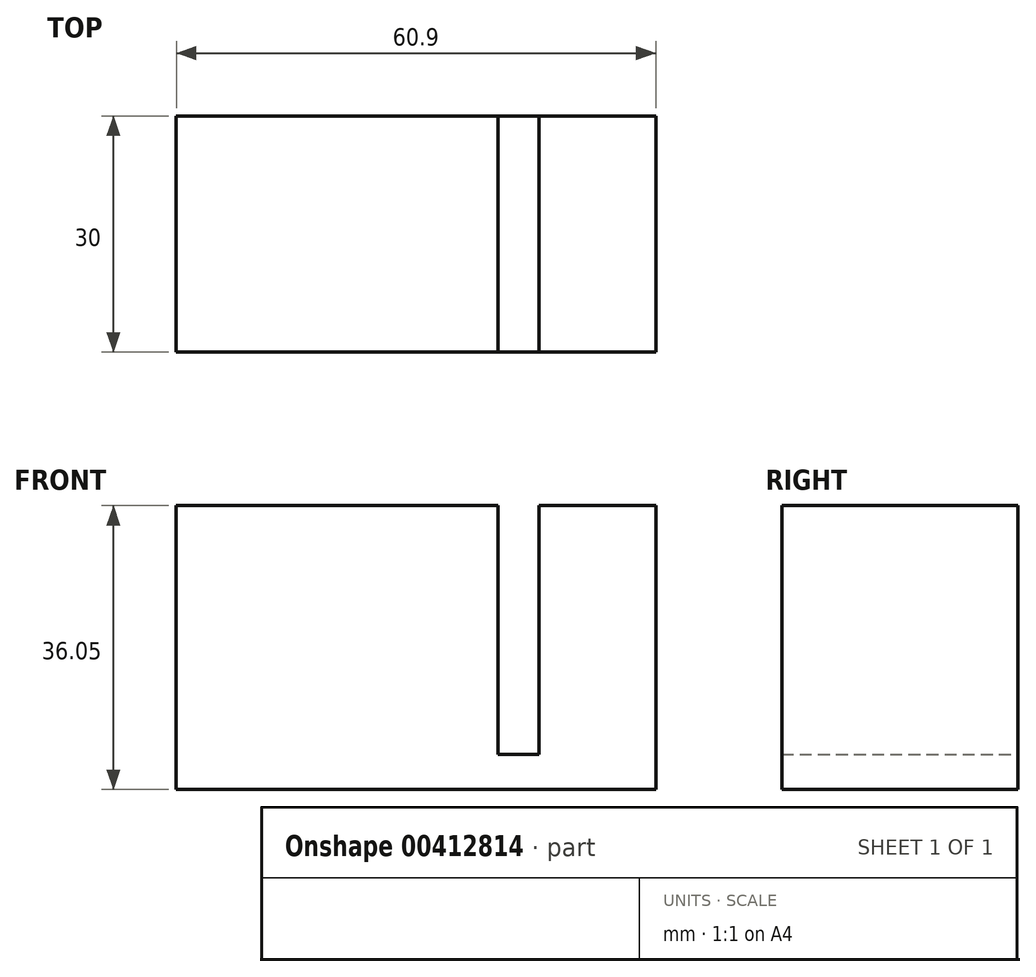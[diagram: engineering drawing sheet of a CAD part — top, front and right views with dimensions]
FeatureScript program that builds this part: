
annotation { "Feature Type Name" : "Feature", "Feature Type Description" : "" }
export const myFeature = defineFeature(function(context is Context, id is Id, definition is map)
    precondition{}
    {
        {
            var Q0;
            Q0=qCreatedBy(makeId("Front.planeOp"),FACE);
            var sketch = newSketch(context, id + "F0", { "sketchPlane" : qUnion([Q0])});
            skLineSegment(sketch, "E0.bottom", {"start": v(0, 0) * mm, "end": v(0, 0) * mm});
            skLineSegment(sketch, "E0.top", {"start": v(0, 0) * mm, "end": v(0, 0) * mm});
            skLineSegment(sketch, "E0.left", {"start": v(0, 0) * mm, "end": v(0, 0) * mm});
            skLineSegment(sketch, "E0.right", {"start": v(0, 0) * mm, "end": v(0, 0) * mm});
            skLineSegment(sketch, "E1.bottom", {"start": v(30.42, 58.1) * mm, "end": v(35.65, 58.1) * mm});
            skLineSegment(sketch, "E1.top", {"start": v(30.42, 20.82) * mm, "end": v(35.65, 20.82) * mm});
            skLineSegment(sketch, "E1.left", {"start": v(30.42, 58.1) * mm, "end": v(30.42, 20.82) * mm});
            skLineSegment(sketch, "E1.right", {"start": v(35.65, 58.1) * mm, "end": v(35.65, 20.82) * mm});
            skLineSegment(sketch, "E2.bottom", {"start": v(-10.41, 52.39) * mm, "end": v(50.49, 52.39) * mm});
            skLineSegment(sketch, "E2.top", {"start": v(-10.41, 16.34) * mm, "end": v(50.49, 16.34) * mm});
            skLineSegment(sketch, "E2.left", {"start": v(-10.41, 52.39) * mm, "end": v(-10.41, 16.34) * mm});
            skLineSegment(sketch, "E2.right", {"start": v(50.49, 52.39) * mm, "end": v(50.49, 16.34) * mm});
            skSolve(sketch);
        }
        {
            var Q0;
            {var subQ1=sQuery(id+"F0.wireOp",EDGE,"E1.top");Q0=makeQuery(id+"F0.imprint","IMPRINT",FACE,{"disambiguationData":[TD([[makeQuery(id+"F0.imprint","IMPRINT",EDGE,{"derivedFrom":subQ1}),-1.0]])]});}
            extrude(context, id + "F1", {"entities" : qUnion([Q0]), "depth" : 30 * mm});
        }
    });
